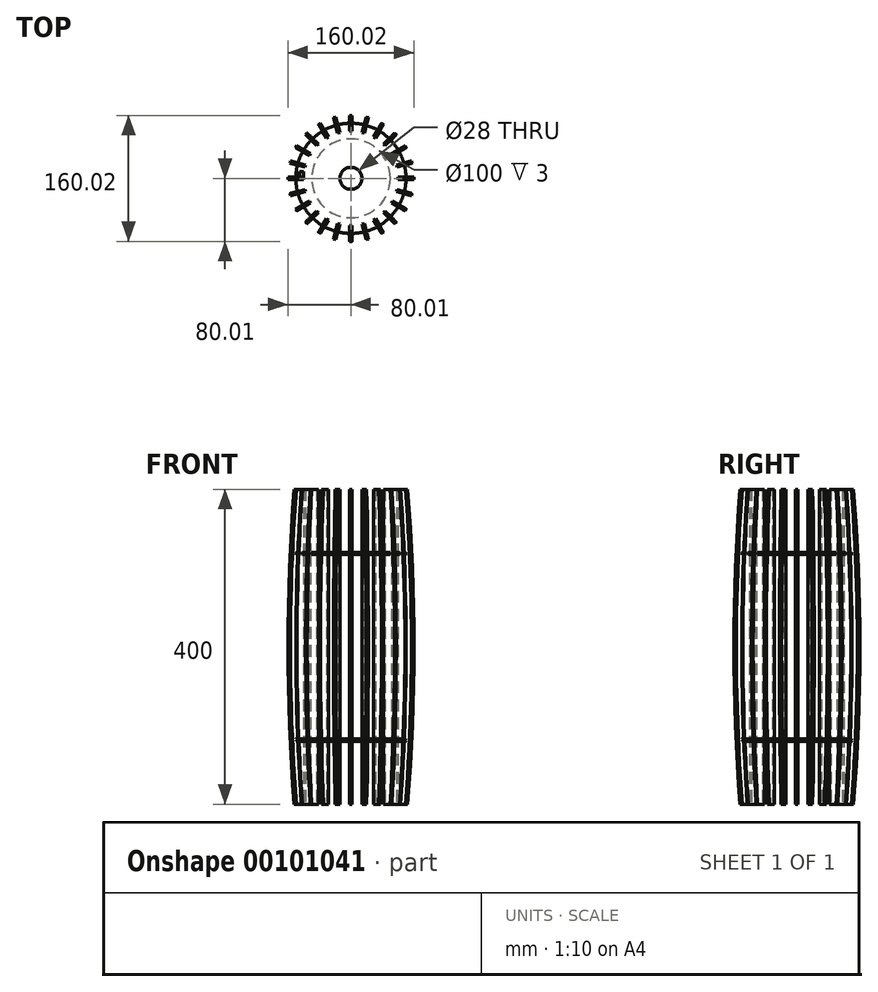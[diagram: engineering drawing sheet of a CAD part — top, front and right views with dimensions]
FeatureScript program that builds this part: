
annotation { "Feature Type Name" : "Feature", "Feature Type Description" : "" }
export const myFeature = defineFeature(function(context is Context, id is Id, definition is map)
    precondition{}
    {
        {
            var Q0;
            Q0=qCreatedBy(makeId("Front.planeOp"),FACE);
            var sketch = newSketch(context, id + "F0", { "sketchPlane" : qUnion([Q0])});
            skLineSegment(sketch, "E0.bottom", {"start": v(-72, 200) * mm, "end": v(-60, 200) * mm});
            skLineSegment(sketch, "E0.top", {"start": v(-72, -200) * mm, "end": v(-60, -200) * mm});
            skLineSegment(sketch, "E0.right", {"start": v(-60, 200) * mm, "end": v(-60, -200) * mm});
            skArc(sketch, "E1", {"start": v(-72, 200) * mm, "mid": v(-80.01, 0) * mm, "end": v(-72, -200) * mm});
            skSolve(sketch);
        }
        {
            var Q0;
            Q0 = qSketchRegion(id + "F0", true);
            extrude(context, id + "F1", {"entities" : qUnion([Q0]), "endBound" : BoundingType.SYMMETRIC, "depth" : 3 * mm});
        }
        {
            var Q0;
            Q0=qCreatedBy(makeId("Top.planeOp"),FACE);
            cPlane(context, id + "F2", {"entities" : qUnion([Q0]), "cplaneType" : CPlaneType.OFFSET, "offset" : 120 * mm, "width" : 150 * mm, "height" : 150 * mm});
        }
        {
            var Q0;
            Q0=qCreatedBy(id+"F2.planeOp",FACE);
            var sketch = newSketch(context, id + "F3", { "sketchPlane" : qUnion([Q0])});
            skCircle(sketch, "E2", {"center": v(0, 0) * mm, "radius": 70 * mm});
            skCircle(sketch, "E3", {"center": v(0, 0) * mm, "radius": 14 * mm});
            skSolve(sketch);
        }
        {
            var Q0;
            Q0=makeQuery(id+"F3.imprint","IMPRINT",FACE,{"disambiguationData":[TD([[makeQuery(id+"F3.imprint","IMPRINT",EDGE,{"derivedFrom":sQuery(id+"F3.wireOp",EDGE,"E2")}),1.0]])]});
            extrude(context, id + "F4", {"entities" : qUnion([Q0]), "oppositeDirection" : true, "depth" : 3 * mm});
        }
        {
            var Q0;
            Q0=makeQuery(id+"F4.opExtrude","CAP_FACE",FACE,{"disambiguationData":[OSD([sQuery(id+"F3.wireOp",EDGE,"E2"),sQuery(id+"F3.wireOp",EDGE,"E3")])],"isStart":true});
            var sketch = newSketch(context, id + "F5", { "sketchPlane" : qUnion([Q0])});
            skLineSegment(sketch, "E4.bottom", {"start": v(-65, -1.5) * mm, "end": v(-72, -1.5) * mm});
            skLineSegment(sketch, "E4.top", {"start": v(-65, 1.5) * mm, "end": v(-72, 1.5) * mm});
            skLineSegment(sketch, "E4.left", {"start": v(-65, -1.5) * mm, "end": v(-65, 1.5) * mm});
            skLineSegment(sketch, "E4.right", {"start": v(-72, -1.5) * mm, "end": v(-72, 1.5) * mm});
            skLineSegment(sketch, "E5", {"start": v(0, 0) * mm, "end": v(-65, 0) * mm, "construction": true});
            skSolve(sketch);
        }
        {
            var Q0;
            Q0 = qSketchRegion(id + "F5", true);
            extrude(context, id + "F6", {"entities" : qUnion([Q0]), "operationType" : NewBodyOperationType.REMOVE, "oppositeDirection" : true, "depth" : 3 * mm});
        }
        {
            var Q0;
            Q0=qCreatedBy(makeId("Front.planeOp"),FACE);
            var sketch = newSketch(context, id + "F7", { "sketchPlane" : qUnion([Q0])});
            skLineSegment(sketch, "E6", {"start": v(0, 0) * mm, "end": v(0, 145.95) * mm, "construction": true});
            skSolve(sketch);
        }
        {
            var Q0;
            Q0=qCreatedBy(makeId("Top.planeOp"),FACE);
            cPlane(context, id + "F8", {"entities" : qUnion([Q0]), "cplaneType" : CPlaneType.OFFSET, "offset" : 120 * mm, "oppositeDirection" : true, "width" : 150 * mm, "height" : 150 * mm});
        }
        {
            var Q0;
            Q0=qCreatedBy(id+"F8.planeOp",FACE);
            var sketch = newSketch(context, id + "F9", { "sketchPlane" : qUnion([Q0])});
            skCircle(sketch, "E7", {"center": v(0, 0) * mm, "radius": 70 * mm});
            skCircle(sketch, "E8", {"center": v(0, 0) * mm, "radius": 50 * mm});
            skSolve(sketch);
        }
        {
            var Q0;
            Q0 = qSketchRegion(id + "F9", true);
            extrude(context, id + "F10", {"entities" : qUnion([Q0]), "depth" : 3 * mm});
        }
        {
            var Q0;
            Q0=makeQuery(id+"F1.opExtrude","CAP_FACE",FACE,{"disambiguationData":[OSD([sQuery(id+"F0.wireOp",EDGE,"E0.bottom"),sQuery(id+"F0.wireOp",EDGE,"E0.top"),sQuery(id+"F0.wireOp",EDGE,"E0.right"),sQuery(id+"F0.wireOp",EDGE,"E1")])],"isStart":false});
            var sketch = newSketch(context, id + "F11", { "sketchPlane" : qUnion([Q0])});
            skLineSegment(sketch, "E9.bottom", {"start": v(-65, 120) * mm, "end": v(-60, 120) * mm});
            skLineSegment(sketch, "E9.top", {"start": v(-65, 117) * mm, "end": v(-60, 117) * mm});
            skLineSegment(sketch, "E9.left", {"start": v(-65, 120) * mm, "end": v(-65, 117) * mm});
            skLineSegment(sketch, "E9.right", {"start": v(-60, 120) * mm, "end": v(-60, 117) * mm});
            skSolve(sketch);
        }
        {
            var Q0;
            Q0 = qSketchRegion(id + "F11", true);
            extrude(context, id + "F12", {"entities" : qUnion([Q0]), "operationType" : NewBodyOperationType.REMOVE, "oppositeDirection" : true, "depth" : 10 * mm});
        }
        {
            var Q0;
            Q0=makeQuery(id+"F1.opExtrude","SWEPT_BODY",BODY,{"disambiguationData":[OSD([sQuery(id+"F0.wireOp",EDGE,"E0.bottom"),sQuery(id+"F0.wireOp",EDGE,"E0.top"),sQuery(id+"F0.wireOp",EDGE,"E0.left"),sQuery(id+"F0.wireOp",EDGE,"E0.right")])]});
            var Q1;
            Q1=sQuery(id+"F7.wireOp",EDGE,"E6");
            circularPattern(context, id + "F13", {"entities" : qUnion([Q0]), "axis" : qUnion([Q1]), "angle" : 360 * degree, "instanceCount" : 24, "equalSpace" : true});
        }
    });
